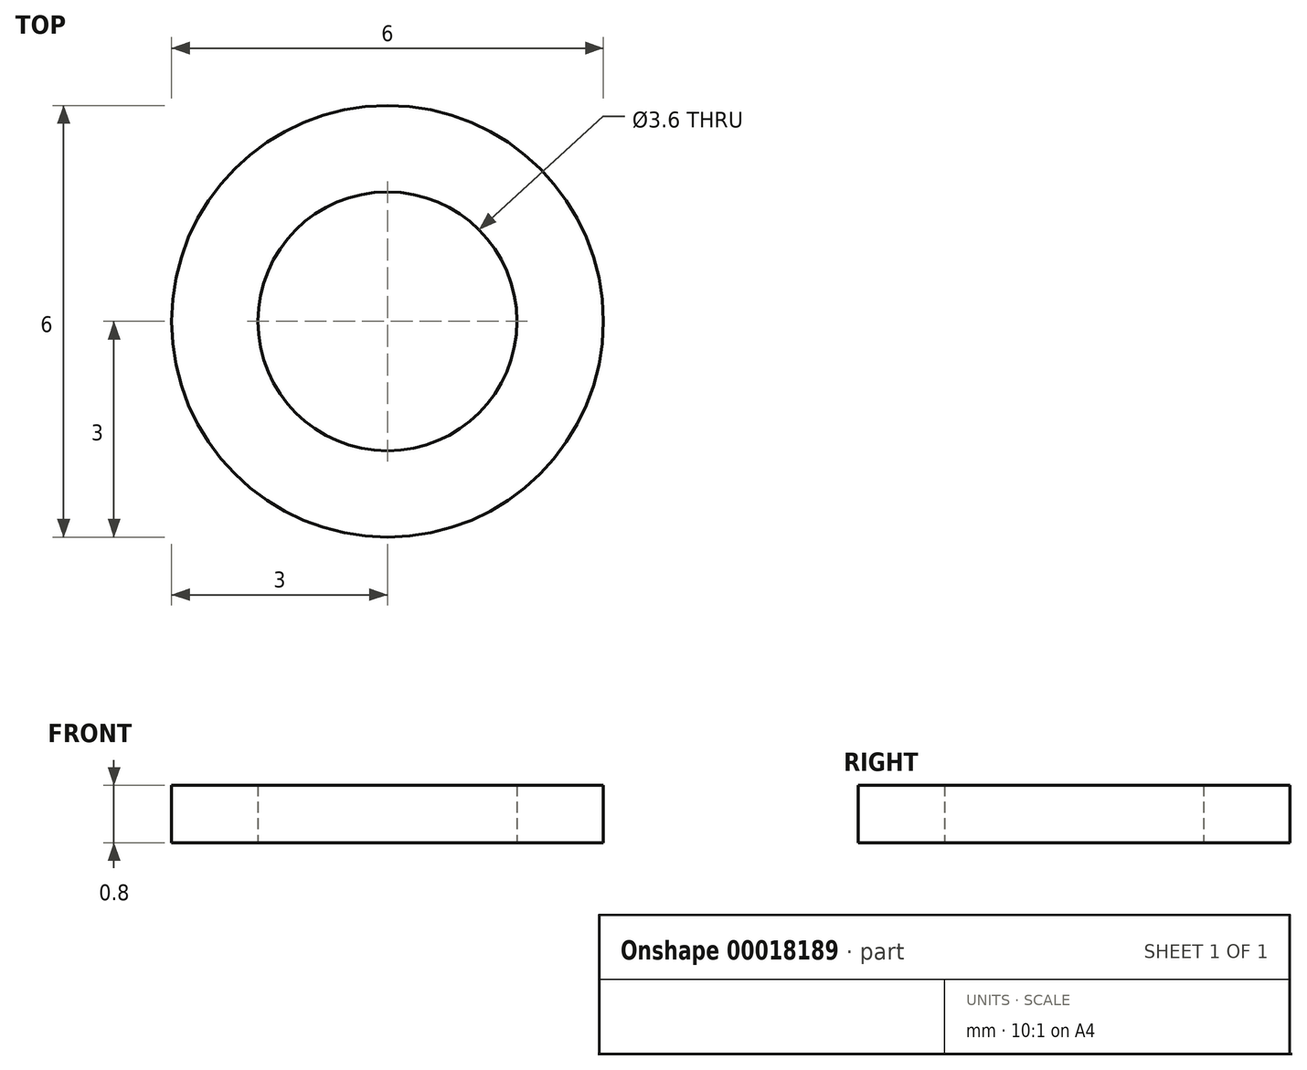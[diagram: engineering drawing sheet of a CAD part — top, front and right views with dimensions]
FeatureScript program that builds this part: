
annotation { "Feature Type Name" : "Feature", "Feature Type Description" : "" }
export const myFeature = defineFeature(function(context is Context, id is Id, definition is map)
    precondition{}
    {
        {
            var Q0;
            Q0=qCreatedBy(makeId("Top.planeOp"),FACE);
            var sketch = newSketch(context, id + "F0", { "sketchPlane" : qUnion([Q0])});
            skCircle(sketch, "E0", {"center": v(0, 0) * mm, "radius": 3 * mm});
            skCircle(sketch, "E1", {"center": v(0, 0) * mm, "radius": 1.8 * mm});
            skSolve(sketch);
        }
        {
            var Q0;
            Q0=makeQuery(id+"F0.imprint","IMPRINT",FACE,{"disambiguationData":[TD([[makeQuery(id+"F0.imprint","IMPRINT",EDGE,{"derivedFrom":sQuery(id+"F0.wireOp",EDGE,"E0")}),1.0]])]});
            extrude(context, id + "F1", {"entities" : qUnion([Q0]), "depth" : 0.8 * mm});
        }
    });
